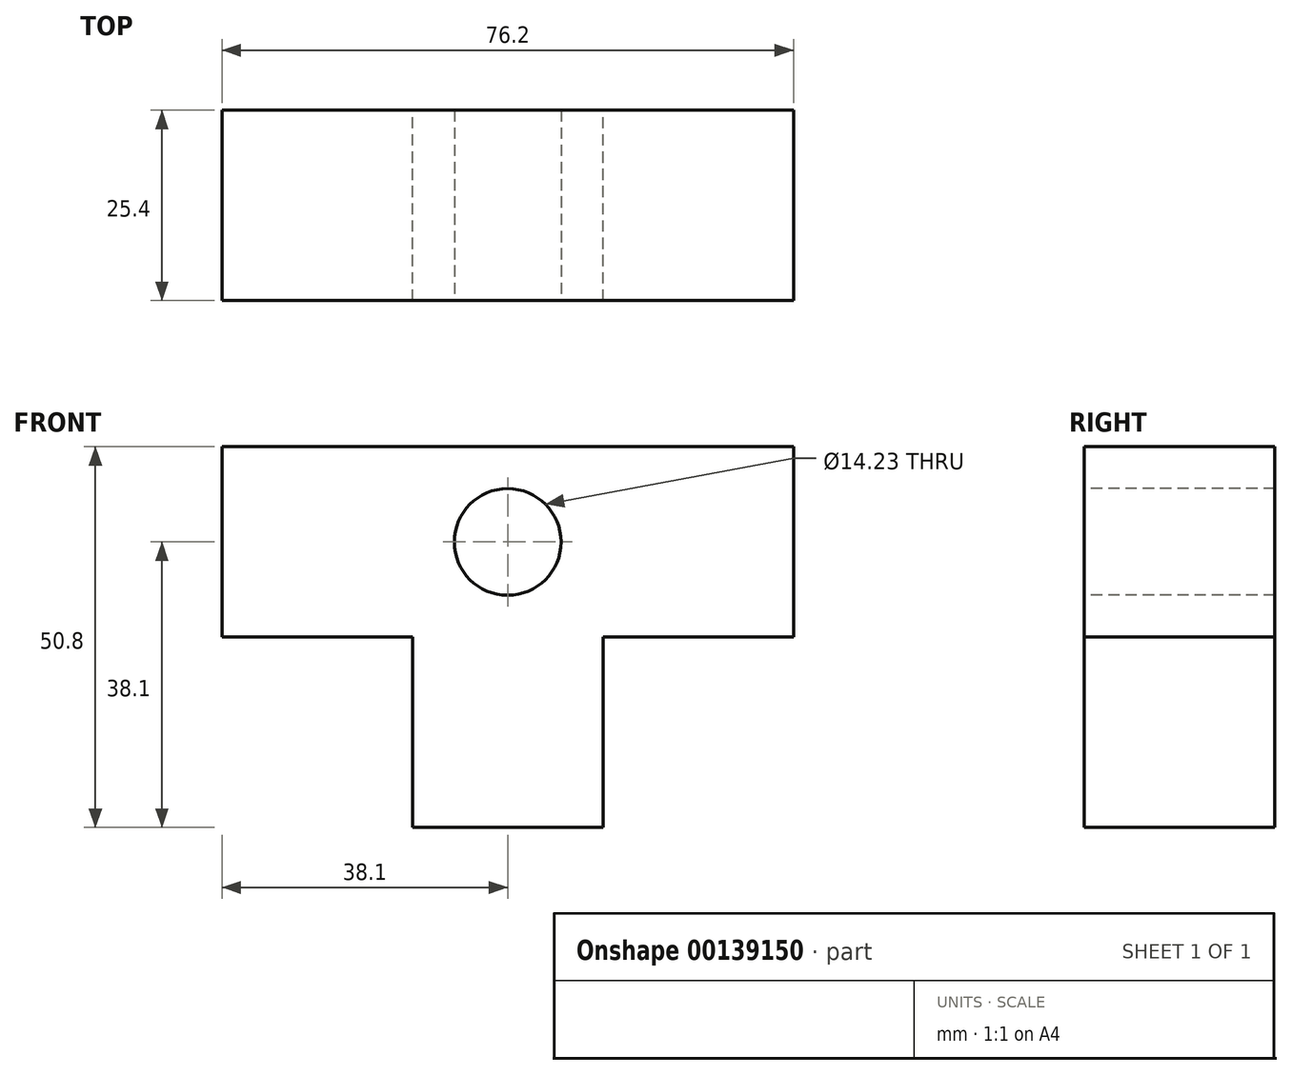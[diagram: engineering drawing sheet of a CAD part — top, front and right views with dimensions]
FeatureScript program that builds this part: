
annotation { "Feature Type Name" : "Feature", "Feature Type Description" : "" }
export const myFeature = defineFeature(function(context is Context, id is Id, definition is map)
    precondition{}
    {
        {
            var Q0;
            Q0=qCreatedBy(makeId("Front.planeOp"),FACE);
            var sketch = newSketch(context, id + "F0", { "sketchPlane" : qUnion([Q0])});
            skLineSegment(sketch, "E0.bottom", {"start": v(12.7, 12.7) * mm, "end": v(-12.7, 12.7) * mm});
            skLineSegment(sketch, "E0.top", {"start": v(12.7, -12.7) * mm, "end": v(-12.7, -12.7) * mm});
            skLineSegment(sketch, "E0.left", {"start": v(12.7, 12.7) * mm, "end": v(12.7, -12.7) * mm});
            skLineSegment(sketch, "E0.right", {"start": v(-12.7, 12.7) * mm, "end": v(-12.7, -12.7) * mm});
            skPoint(sketch, "E0.middle", {"position": v(0, 0) * mm});
            skLineSegment(sketch, "E1.bottom", {"start": v(-12.7, 12.7) * mm, "end": v(-38.1, 12.7) * mm});
            skLineSegment(sketch, "E1.top", {"start": v(-12.7, -12.7) * mm, "end": v(-38.1, -12.7) * mm});
            skLineSegment(sketch, "E1.right", {"start": v(-38.1, 12.7) * mm, "end": v(-38.1, -12.7) * mm});
            skLineSegment(sketch, "E2.bottom", {"start": v(12.7, 12.7) * mm, "end": v(38.1, 12.7) * mm});
            skLineSegment(sketch, "E2.top", {"start": v(12.7, -12.7) * mm, "end": v(38.1, -12.7) * mm});
            skLineSegment(sketch, "E2.right", {"start": v(38.1, 12.7) * mm, "end": v(38.1, -12.7) * mm});
            skLineSegment(sketch, "E3.top", {"start": v(12.7, -38.1) * mm, "end": v(-12.7, -38.1) * mm});
            skLineSegment(sketch, "E3.left", {"start": v(12.7, -12.7) * mm, "end": v(12.7, -38.1) * mm});
            skLineSegment(sketch, "E3.right", {"start": v(-12.7, -12.7) * mm, "end": v(-12.7, -38.1) * mm});
            skSolve(sketch);
        }
        {
            var Q0;
            Q0=makeQuery(id+"F0.imprint","IMPRINT",FACE,{"disambiguationData":[TD([[makeQuery(id+"F0.imprint","IMPRINT",EDGE,{"derivedFrom":sQuery(id+"F0.wireOp",EDGE,"E1.bottom")}),1.0]])]});
            var Q1;
            Q1=makeQuery(id+"F0.imprint","IMPRINT",FACE,{"disambiguationData":[TD([[makeQuery(id+"F0.imprint","IMPRINT",EDGE,{"derivedFrom":sQuery(id+"F0.wireOp",EDGE,"E0.bottom")}),1.0]])]});
            var Q2;
            Q2=makeQuery(id+"F0.imprint","IMPRINT",FACE,{"disambiguationData":[TD([[makeQuery(id+"F0.imprint","IMPRINT",EDGE,{"derivedFrom":sQuery(id+"F0.wireOp",EDGE,"E2.bottom")}),-1.0]])]});
            var Q3;
            Q3=makeQuery(id+"F0.imprint","IMPRINT",FACE,{"disambiguationData":[TD([[makeQuery(id+"F0.imprint","IMPRINT",EDGE,{"derivedFrom":sQuery(id+"F0.wireOp",EDGE,"E0.top")}),1.0]])]});
            extrude(context, id + "F1", {"entities" : qUnion([Q0, Q1, Q2, Q3]), "depth" : 25.4 * mm});
        }
        {
            var Q0;
            Q0=makeQuery(id+"F1.opExtrude","CAP_FACE",FACE,{"disambiguationData":[OSD([sQuery(id+"F0.wireOp",EDGE,"E0.bottom"),sQuery(id+"F0.wireOp",EDGE,"E1.bottom"),sQuery(id+"F0.wireOp",EDGE,"E1.top"),sQuery(id+"F0.wireOp",EDGE,"E1.right"),sQuery(id+"F0.wireOp",EDGE,"E2.bottom"),sQuery(id+"F0.wireOp",EDGE,"E2.top"),sQuery(id+"F0.wireOp",EDGE,"E2.right"),sQuery(id+"F0.wireOp",EDGE,"E3.top"),sQuery(id+"F0.wireOp",EDGE,"E3.left"),sQuery(id+"F0.wireOp",EDGE,"E3.right")])],"isStart":false});
            var sketch = newSketch(context, id + "F2", { "sketchPlane" : qUnion([Q0])});
            skCircle(sketch, "E4", {"center": v(0, 0) * mm, "radius": 7.11 * mm});
            skSolve(sketch);
        }
        {
            var Q0;
            Q0=makeQuery(id+"F2.imprint","IMPRINT",FACE,{"disambiguationData":[TD([[makeQuery(id+"F2.imprint","IMPRINT",EDGE,{"derivedFrom":sQuery(id+"F2.wireOp",EDGE,"E4")}),1.0]])]});
            extrude(context, id + "F3", {"entities" : qUnion([Q0]), "operationType" : NewBodyOperationType.REMOVE, "oppositeDirection" : true, "depth" : 25.4 * mm});
        }
    });
